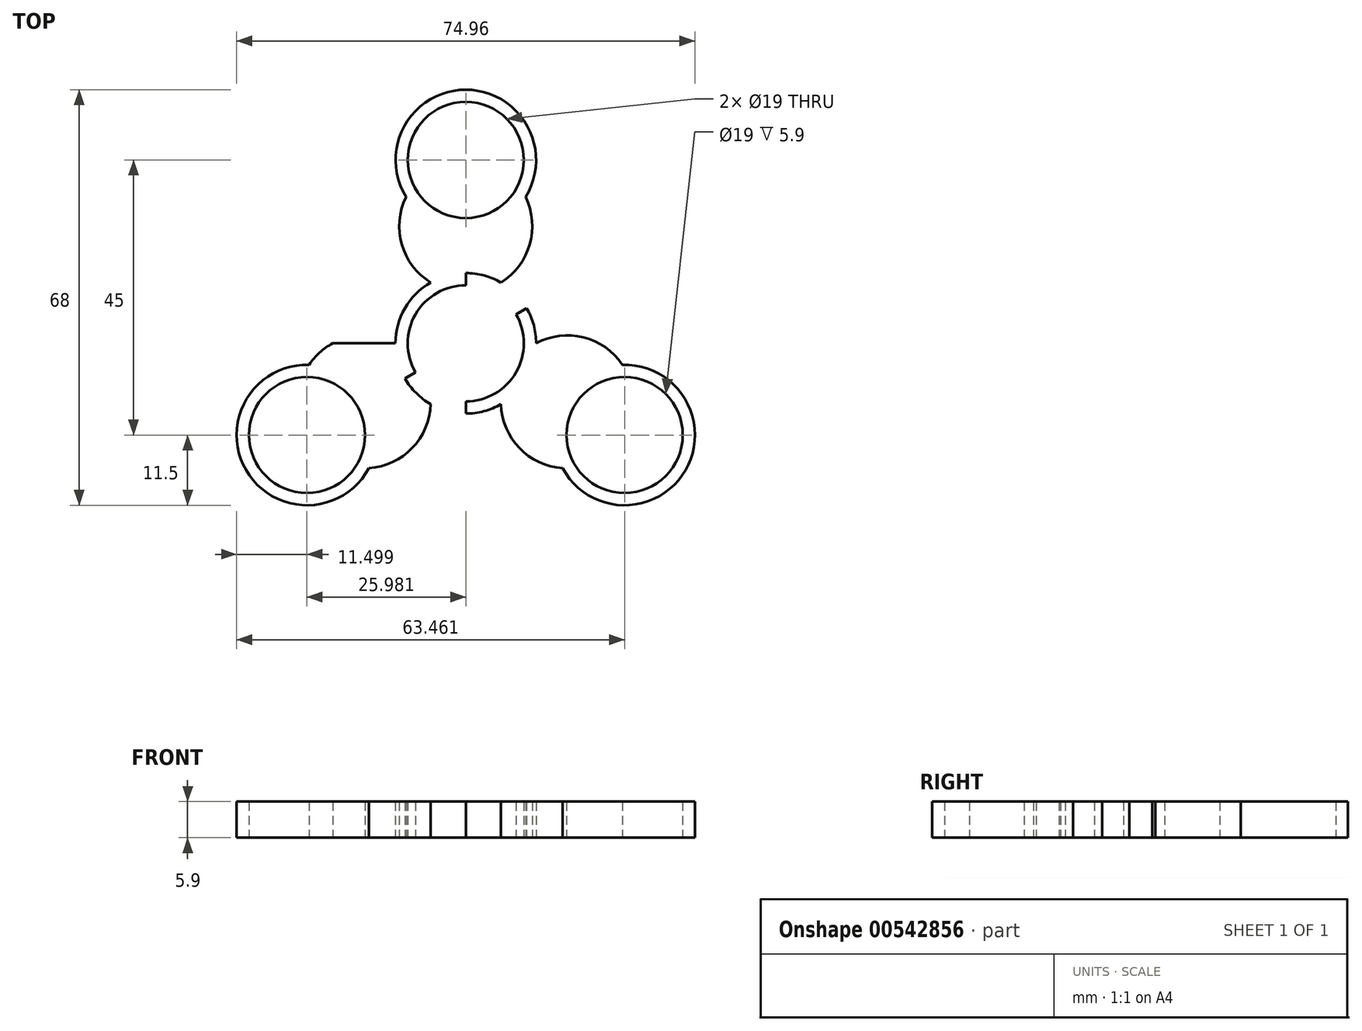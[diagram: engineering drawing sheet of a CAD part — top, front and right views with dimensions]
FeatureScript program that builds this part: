
annotation { "Feature Type Name" : "Feature", "Feature Type Description" : "" }
export const myFeature = defineFeature(function(context is Context, id is Id, definition is map)
    precondition{}
    {
        {
            var Q0;
            Q0=qCreatedBy(makeId("Top.planeOp"),FACE);
            var sketch = newSketch(context, id + "F0", { "sketchPlane" : qUnion([Q0])});
            skCircle(sketch, "E0", {"center": v(0, 0) * mm, "radius": 9.5 * mm});
            skCircle(sketch, "E1", {"center": v(0, 0) * mm, "radius": 11.5 * mm});
            skLineSegment(sketch, "E2", {"start": v(0, 0) * mm, "end": v(0, 30) * mm});
            skLineSegment(sketch, "E3.1.0", {"start": v(0, 0) * mm, "end": v(-25.98, -15) * mm});
            skLineSegment(sketch, "E3.2.0", {"start": v(0, 0) * mm, "end": v(25.98, -15) * mm});
            skCircle(sketch, "E4", {"center": v(0, 30) * mm, "radius": 9.5 * mm});
            skCircle(sketch, "E5", {"center": v(0, 30) * mm, "radius": 11.5 * mm});
            skCircle(sketch, "E6", {"center": v(-25.98, -15) * mm, "radius": 11.5 * mm});
            skCircle(sketch, "E7", {"center": v(-25.98, -15) * mm, "radius": 9.5 * mm});
            skCircle(sketch, "E8", {"center": v(25.98, -15) * mm, "radius": 9.5 * mm});
            skCircle(sketch, "E9", {"center": v(25.98, -15) * mm, "radius": 11.5 * mm});
            skLineSegment(sketch, "E10", {"start": v(0, 0) * mm, "end": v(-40.42, 0) * mm});
            skLineSegment(sketch, "E11", {"start": v(-40.42, 0) * mm, "end": v(44.58, 0) * mm});
            skLineSegment(sketch, "E12", {"start": v(0, 0) * mm, "end": v(0, -28.13) * mm});
            skLineSegment(sketch, "E13", {"start": v(0, 0) * mm, "end": v(35.38, 20.43) * mm});
            skLineSegment(sketch, "E14", {"start": v(35.38, 20.43) * mm, "end": v(0, 0) * mm});
            skLineSegment(sketch, "E15", {"start": v(0, 0) * mm, "end": v(-40.5, 23.39) * mm});
            skArc(sketch, "E16", {"start": v(-11.5, 0) * mm, "mid": v(-24.42, -2.01) * mm, "end": v(-25.98, -15) * mm});
            skArc(sketch, "E17.MirrorCS", {"start": v(-5.75, -9.96) * mm, "mid": v(-13.96, -20.14) * mm, "end": v(-25.98, -15) * mm});
            skArc(sketch, "E18.MirrorCS", {"start": v(5.75, -9.96) * mm, "mid": v(13.96, -20.14) * mm, "end": v(25.98, -15) * mm});
            skArc(sketch, "E19.MirrorCS", {"start": v(11.5, 0) * mm, "mid": v(24.42, -2.01) * mm, "end": v(25.98, -15) * mm});
            skArc(sketch, "E20.MirrorCS", {"start": v(-5.75, 9.96) * mm, "mid": v(-10.47, 22.16) * mm, "end": v(0, 30) * mm});
            skArc(sketch, "E21.MirrorCS", {"start": v(5.75, 9.96) * mm, "mid": v(10.47, 22.16) * mm, "end": v(0, 30) * mm});
            skSolve(sketch);
        }
        {
            var Q0;
            {var subQ0=sQuery(id+"F0.wireOp",EDGE,"E16");var subQ1=sQuery(id+"F0.wireOp",EDGE,"E6");var subQ2=makeQuery(id+"F0.imprint","INTERSECT",VERTEX,{"derivedFrom":[subQ1,subQ0]});Q0=makeQuery(id+"F0.imprint","IMPRINT",FACE,{"disambiguationData":[TD([[makeQuery(id+"F0.imprint","IMPRINT",EDGE,{"disambiguationData":[TD([[subQ2,-1.0]])],"derivedFrom":subQ1}),1.0]])]});}
            var Q1;
            {var subQ0=sQuery(id+"F0.wireOp",EDGE,"E17.MirrorCS");var subQ1=sQuery(id+"F0.wireOp",EDGE,"E1");var subQ2=makeQuery(id+"F0.imprint","INTERSECT",VERTEX,{"derivedFrom":[subQ1,subQ0]});Q1=makeQuery(id+"F0.imprint","IMPRINT",FACE,{"disambiguationData":[TD([[makeQuery(id+"F0.imprint","IMPRINT",EDGE,{"disambiguationData":[TD([[subQ2,1.0]])],"derivedFrom":subQ1}),-1.0]])]});}
            var Q2;
            {var subQ0=sQuery(id+"F0.wireOp",EDGE,"E16");var subQ5=sQuery(id+"F0.wireOp",EDGE,"E6");var subQ6=makeQuery(id+"F0.imprint","INTERSECT",VERTEX,{"derivedFrom":[subQ5,subQ0]});Q2=makeQuery(id+"F0.imprint","IMPRINT",FACE,{"disambiguationData":[TD([[makeQuery(id+"F0.imprint","IMPRINT",EDGE,{"disambiguationData":[TD([[subQ6,1.0]])],"derivedFrom":subQ5}),-1.0]])]});}
            var Q3;
            {var subQ0=sQuery(id+"F0.wireOp",EDGE,"E16");var subQ1=sQuery(id+"F0.wireOp",EDGE,"E6");var subQ2=makeQuery(id+"F0.imprint","INTERSECT",VERTEX,{"derivedFrom":[subQ1,subQ0]});Q3=makeQuery(id+"F0.imprint","IMPRINT",FACE,{"disambiguationData":[TD([[makeQuery(id+"F0.imprint","IMPRINT",EDGE,{"disambiguationData":[TD([[subQ2,1.0]])],"derivedFrom":subQ1}),1.0]])]});}
            var Q4;
            {var subQ0=sQuery(id+"F0.wireOp",EDGE,"E17.MirrorCS");var subQ1=sQuery(id+"F0.wireOp",EDGE,"E6");var subQ2=makeQuery(id+"F0.imprint","INTERSECT",VERTEX,{"derivedFrom":[subQ1,subQ0]});Q4=makeQuery(id+"F0.imprint","IMPRINT",FACE,{"disambiguationData":[TD([[makeQuery(id+"F0.imprint","IMPRINT",EDGE,{"disambiguationData":[TD([[subQ2,-1.0]])],"derivedFrom":subQ1}),1.0]])]});}
            var Q5;
            {var subQ0=sQuery(id+"F0.wireOp",EDGE,"E9");var subQ1=sQuery(id+"F0.wireOp",EDGE,"E3.2.0");var subQ2=makeQuery(id+"F0.imprint","INTERSECT",VERTEX,{"derivedFrom":[subQ1,subQ0]});Q5=makeQuery(id+"F0.imprint","IMPRINT",FACE,{"disambiguationData":[TD([[makeQuery(id+"F0.imprint","IMPRINT",EDGE,{"disambiguationData":[TD([[subQ2,-1.0]])],"derivedFrom":subQ1}),-1.0]])]});}
            var Q6;
            {var subQ0=sQuery(id+"F0.wireOp",EDGE,"E18.MirrorCS");var subQ1=sQuery(id+"F0.wireOp",EDGE,"E1");var subQ2=makeQuery(id+"F0.imprint","INTERSECT",VERTEX,{"derivedFrom":[subQ1,subQ0]});Q6=makeQuery(id+"F0.imprint","IMPRINT",FACE,{"disambiguationData":[TD([[makeQuery(id+"F0.imprint","IMPRINT",EDGE,{"disambiguationData":[TD([[subQ2,-1.0]])],"derivedFrom":subQ1}),-1.0]])]});}
            var Q7;
            {var subQ2=sQuery(id+"F0.wireOp",EDGE,"E1");var subQ7=sQuery(id+"F0.wireOp",EDGE,"E3.2.0");var subQ9=makeQuery(id+"F0.imprint","INTERSECT",VERTEX,{"derivedFrom":[subQ2,subQ7]});Q7=makeQuery(id+"F0.imprint","IMPRINT",FACE,{"disambiguationData":[TD([[makeQuery(id+"F0.imprint","IMPRINT",EDGE,{"disambiguationData":[TD([[subQ9,-1.0]])],"derivedFrom":subQ7}),1.0]])]});}
            var Q8;
            {var subQ0=sQuery(id+"F0.wireOp",EDGE,"E19.MirrorCS");var subQ1=sQuery(id+"F0.wireOp",EDGE,"E8");var subQ2=makeQuery(id+"F0.imprint","INTERSECT",VERTEX,{"derivedFrom":[subQ1,subQ0]});Q8=makeQuery(id+"F0.imprint","IMPRINT",FACE,{"disambiguationData":[TD([[makeQuery(id+"F0.imprint","IMPRINT",EDGE,{"disambiguationData":[TD([[subQ2,1.0]])],"derivedFrom":subQ1}),-1.0]])]});}
            var Q9;
            {var subQ0=sQuery(id+"F0.wireOp",EDGE,"E9");var subQ1=sQuery(id+"F0.wireOp",EDGE,"E3.2.0");var subQ2=makeQuery(id+"F0.imprint","INTERSECT",VERTEX,{"derivedFrom":[subQ1,subQ0]});Q9=makeQuery(id+"F0.imprint","IMPRINT",FACE,{"disambiguationData":[TD([[makeQuery(id+"F0.imprint","IMPRINT",EDGE,{"disambiguationData":[TD([[subQ2,-1.0]])],"derivedFrom":subQ1}),1.0]])]});}
            var Q10;
            {var subQ4=sQuery(id+"F0.wireOp",EDGE,"E0");var subQ6=sQuery(id+"F0.wireOp",EDGE,"E14");var subQ8=makeQuery(id+"F0.imprint","INTERSECT",VERTEX,{"derivedFrom":[subQ4,subQ6]});Q10=makeQuery(id+"F0.imprint","IMPRINT",FACE,{"disambiguationData":[TD([[makeQuery(id+"F0.imprint","IMPRINT",EDGE,{"disambiguationData":[TD([[subQ8,-1.0]])],"derivedFrom":subQ4}),-1.0]])]});}
            var Q11;
            {var subQ0=sQuery(id+"F0.wireOp",EDGE,"E14");var subQ1=sQuery(id+"F0.wireOp",EDGE,"E0");var subQ2=makeQuery(id+"F0.imprint","INTERSECT",VERTEX,{"derivedFrom":[subQ1,subQ0]});Q11=makeQuery(id+"F0.imprint","IMPRINT",FACE,{"disambiguationData":[TD([[makeQuery(id+"F0.imprint","IMPRINT",EDGE,{"disambiguationData":[TD([[subQ2,1.0]])],"derivedFrom":subQ1}),-1.0]])]});}
            var Q12;
            {var subQ0=sQuery(id+"F0.wireOp",EDGE,"E11");var subQ1=sQuery(id+"F0.wireOp",EDGE,"E0");var subQ2=makeQuery(id+"F0.imprint","INTERSECT",VERTEX,{"disambiguationData":[OD(0.0)],"derivedFrom":[subQ1,subQ0]});Q12=makeQuery(id+"F0.imprint","IMPRINT",FACE,{"disambiguationData":[TD([[makeQuery(id+"F0.imprint","IMPRINT",EDGE,{"disambiguationData":[TD([[subQ2,1.0]])],"derivedFrom":subQ1}),-1.0]])]});}
            var Q13;
            {var subQ4=sQuery(id+"F0.wireOp",EDGE,"E12");var subQ6=sQuery(id+"F0.wireOp",EDGE,"E0");var subQ7=makeQuery(id+"F0.imprint","INTERSECT",VERTEX,{"derivedFrom":[subQ6,subQ4]});Q13=makeQuery(id+"F0.imprint","IMPRINT",FACE,{"disambiguationData":[TD([[makeQuery(id+"F0.imprint","IMPRINT",EDGE,{"disambiguationData":[TD([[subQ7,-1.0]])],"derivedFrom":subQ6}),-1.0]])]});}
            var Q14;
            {var subQ4=sQuery(id+"F0.wireOp",EDGE,"E3.1.0");var subQ5=sQuery(id+"F0.wireOp",EDGE,"E0");var subQ6=makeQuery(id+"F0.imprint","INTERSECT",VERTEX,{"derivedFrom":[subQ5,subQ4]});Q14=makeQuery(id+"F0.imprint","IMPRINT",FACE,{"disambiguationData":[TD([[makeQuery(id+"F0.imprint","IMPRINT",EDGE,{"disambiguationData":[TD([[subQ6,-1.0]])],"derivedFrom":subQ5}),-1.0]])]});}
            var Q15;
            {var subQ0=sQuery(id+"F0.wireOp",EDGE,"E11");var subQ1=sQuery(id+"F0.wireOp",EDGE,"E0");var subQ2=makeQuery(id+"F0.imprint","INTERSECT",VERTEX,{"disambiguationData":[OD(1.0)],"derivedFrom":[subQ1,subQ0]});Q15=makeQuery(id+"F0.imprint","IMPRINT",FACE,{"disambiguationData":[TD([[makeQuery(id+"F0.imprint","IMPRINT",EDGE,{"disambiguationData":[TD([[subQ2,-1.0]])],"derivedFrom":subQ1}),-1.0]])]});}
            var Q16;
            {var subQ0=sQuery(id+"F0.wireOp",EDGE,"E15");var subQ1=sQuery(id+"F0.wireOp",EDGE,"E0");var subQ2=makeQuery(id+"F0.imprint","INTERSECT",VERTEX,{"derivedFrom":[subQ1,subQ0]});Q16=makeQuery(id+"F0.imprint","IMPRINT",FACE,{"disambiguationData":[TD([[makeQuery(id+"F0.imprint","IMPRINT",EDGE,{"disambiguationData":[TD([[subQ2,-1.0]])],"derivedFrom":subQ1}),-1.0]])]});}
            var Q17;
            {var subQ0=sQuery(id+"F0.wireOp",EDGE,"E2");var subQ1=sQuery(id+"F0.wireOp",EDGE,"E0");var subQ2=makeQuery(id+"F0.imprint","INTERSECT",VERTEX,{"derivedFrom":[subQ1,subQ0]});Q17=makeQuery(id+"F0.imprint","IMPRINT",FACE,{"disambiguationData":[TD([[makeQuery(id+"F0.imprint","IMPRINT",EDGE,{"disambiguationData":[TD([[subQ2,-1.0]])],"derivedFrom":subQ1}),-1.0]])]});}
            var Q18;
            {var subQ0=sQuery(id+"F0.wireOp",EDGE,"E20.MirrorCS");var subQ1=sQuery(id+"F0.wireOp",EDGE,"E1");var subQ2=makeQuery(id+"F0.imprint","INTERSECT",VERTEX,{"derivedFrom":[subQ1,subQ0]});Q18=makeQuery(id+"F0.imprint","IMPRINT",FACE,{"disambiguationData":[TD([[makeQuery(id+"F0.imprint","IMPRINT",EDGE,{"disambiguationData":[TD([[subQ2,1.0]])],"derivedFrom":subQ1}),-1.0]])]});}
            var Q19;
            {var subQ0=sQuery(id+"F0.wireOp",EDGE,"E21.MirrorCS");var subQ1=sQuery(id+"F0.wireOp",EDGE,"E1");var subQ2=makeQuery(id+"F0.imprint","INTERSECT",VERTEX,{"derivedFrom":[subQ1,subQ0]});Q19=makeQuery(id+"F0.imprint","IMPRINT",FACE,{"disambiguationData":[TD([[makeQuery(id+"F0.imprint","IMPRINT",EDGE,{"disambiguationData":[TD([[subQ2,-1.0]])],"derivedFrom":subQ1}),-1.0]])]});}
            var Q20;
            {var subQ0=sQuery(id+"F0.wireOp",EDGE,"E5");var subQ1=sQuery(id+"F0.wireOp",EDGE,"E2");var subQ2=makeQuery(id+"F0.imprint","INTERSECT",VERTEX,{"derivedFrom":[subQ1,subQ0]});Q20=makeQuery(id+"F0.imprint","IMPRINT",FACE,{"disambiguationData":[TD([[makeQuery(id+"F0.imprint","IMPRINT",EDGE,{"disambiguationData":[TD([[subQ2,-1.0]])],"derivedFrom":subQ1}),-1.0]])]});}
            var Q21;
            {var subQ0=sQuery(id+"F0.wireOp",EDGE,"E5");var subQ1=sQuery(id+"F0.wireOp",EDGE,"E2");var subQ2=makeQuery(id+"F0.imprint","INTERSECT",VERTEX,{"derivedFrom":[subQ1,subQ0]});Q21=makeQuery(id+"F0.imprint","IMPRINT",FACE,{"disambiguationData":[TD([[makeQuery(id+"F0.imprint","IMPRINT",EDGE,{"disambiguationData":[TD([[subQ2,-1.0]])],"derivedFrom":subQ1}),1.0]])]});}
            var Q22;
            {var subQ0=sQuery(id+"F0.wireOp",EDGE,"E20.MirrorCS");var subQ1=sQuery(id+"F0.wireOp",EDGE,"E4");var subQ2=makeQuery(id+"F0.imprint","INTERSECT",VERTEX,{"derivedFrom":[subQ1,subQ0]});Q22=makeQuery(id+"F0.imprint","IMPRINT",FACE,{"disambiguationData":[TD([[makeQuery(id+"F0.imprint","IMPRINT",EDGE,{"disambiguationData":[TD([[subQ2,1.0]])],"derivedFrom":subQ1}),-1.0]])]});}
            var Q23;
            {var subQ0=sQuery(id+"F0.wireOp",EDGE,"E19.MirrorCS");var subQ1=sQuery(id+"F0.wireOp",EDGE,"E11");var subQ3=makeQuery(id+"F0.imprint","INTERSECT",VERTEX,{"derivedFrom":[subQ1,subQ0]});Q23=makeQuery(id+"F0.imprint","IMPRINT",FACE,{"disambiguationData":[TD([[makeQuery(id+"F0.imprint","IMPRINT",EDGE,{"disambiguationData":[TD([[subQ3,1.0]])],"derivedFrom":subQ1}),1.0]])]});}
            var Q24;
            {var subQ0=sQuery(id+"F0.wireOp",EDGE,"E16");var subQ1=sQuery(id+"F0.wireOp",EDGE,"E11");var subQ3=makeQuery(id+"F0.imprint","INTERSECT",VERTEX,{"derivedFrom":[subQ1,subQ0]});Q24=makeQuery(id+"F0.imprint","IMPRINT",FACE,{"disambiguationData":[TD([[makeQuery(id+"F0.imprint","IMPRINT",EDGE,{"disambiguationData":[TD([[subQ3,-1.0]])],"derivedFrom":subQ1}),1.0]])]});}
            extrude(context, id + "F1", {"entities" : qUnion([Q0, Q1, Q2, Q3, Q4, Q5, Q6, Q7, Q8, Q9, Q10, Q11, Q12, Q13, Q14, Q15, Q16, Q17, Q18, Q19, Q20, Q21, Q22, Q23, Q24]), "depth" : 5.9 * mm, "offsetDistance" : 25 * mm});
        }
    });
